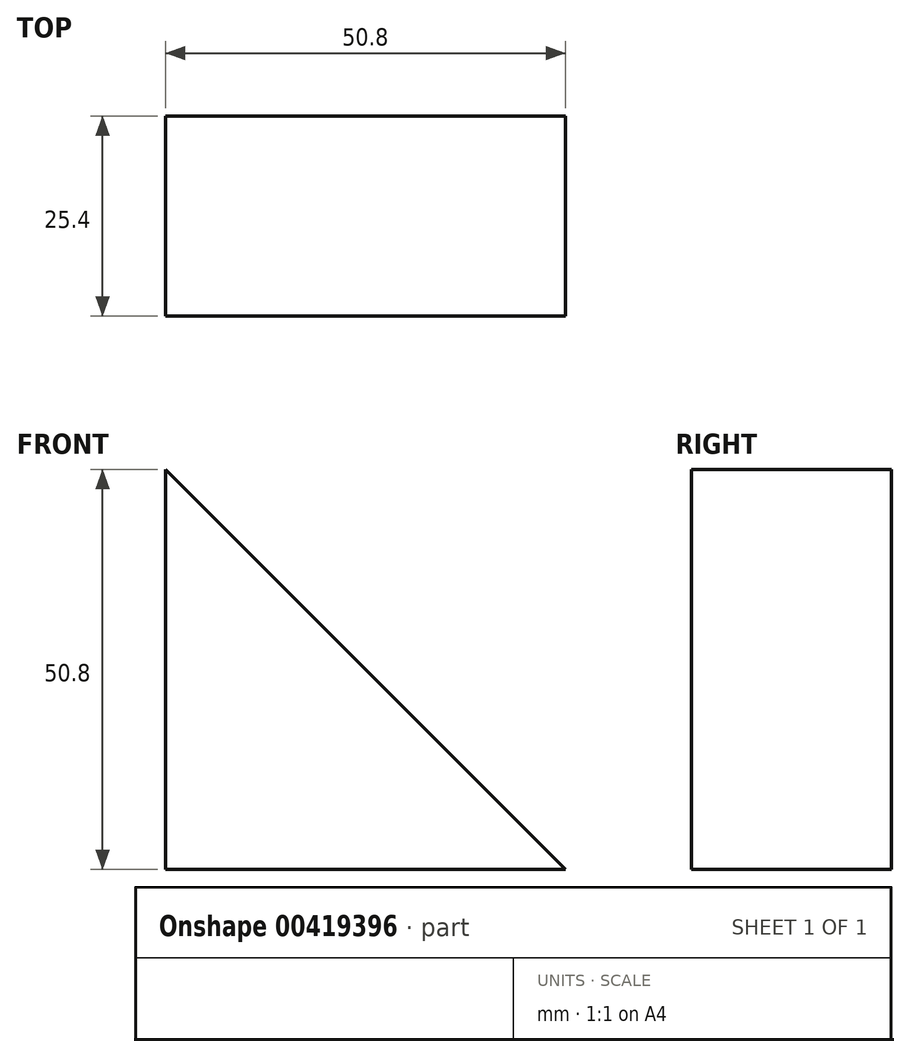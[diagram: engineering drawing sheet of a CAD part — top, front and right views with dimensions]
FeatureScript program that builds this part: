
annotation { "Feature Type Name" : "Feature", "Feature Type Description" : "" }
export const myFeature = defineFeature(function(context is Context, id is Id, definition is map)
    precondition{}
    {
        {
            var Q0;
            Q0=qCreatedBy(makeId("Front.planeOp"),FACE);
            var sketch = newSketch(context, id + "F0", { "sketchPlane" : qUnion([Q0])});
            skLineSegment(sketch, "E0", {"start": v(0, 0) * mm, "end": v(-50.8, 0) * mm});
            skLineSegment(sketch, "E1", {"start": v(-50.8, 0) * mm, "end": v(-50.8, 50.8) * mm});
            skLineSegment(sketch, "E2", {"start": v(-50.8, 50.8) * mm, "end": v(0, 0) * mm});
            skLineSegment(sketch, "E3", {"start": v(-37.62, 22.53) * mm, "end": v(-126.41, 73.7) * mm});
            skSolve(sketch);
        }
        {
            var Q0;
            Q0 = qSketchRegion(id + "F0", true);
            extrude(context, id + "F1", {"entities" : qUnion([Q0]), "depth" : 25.4 * mm});
        }
    });
